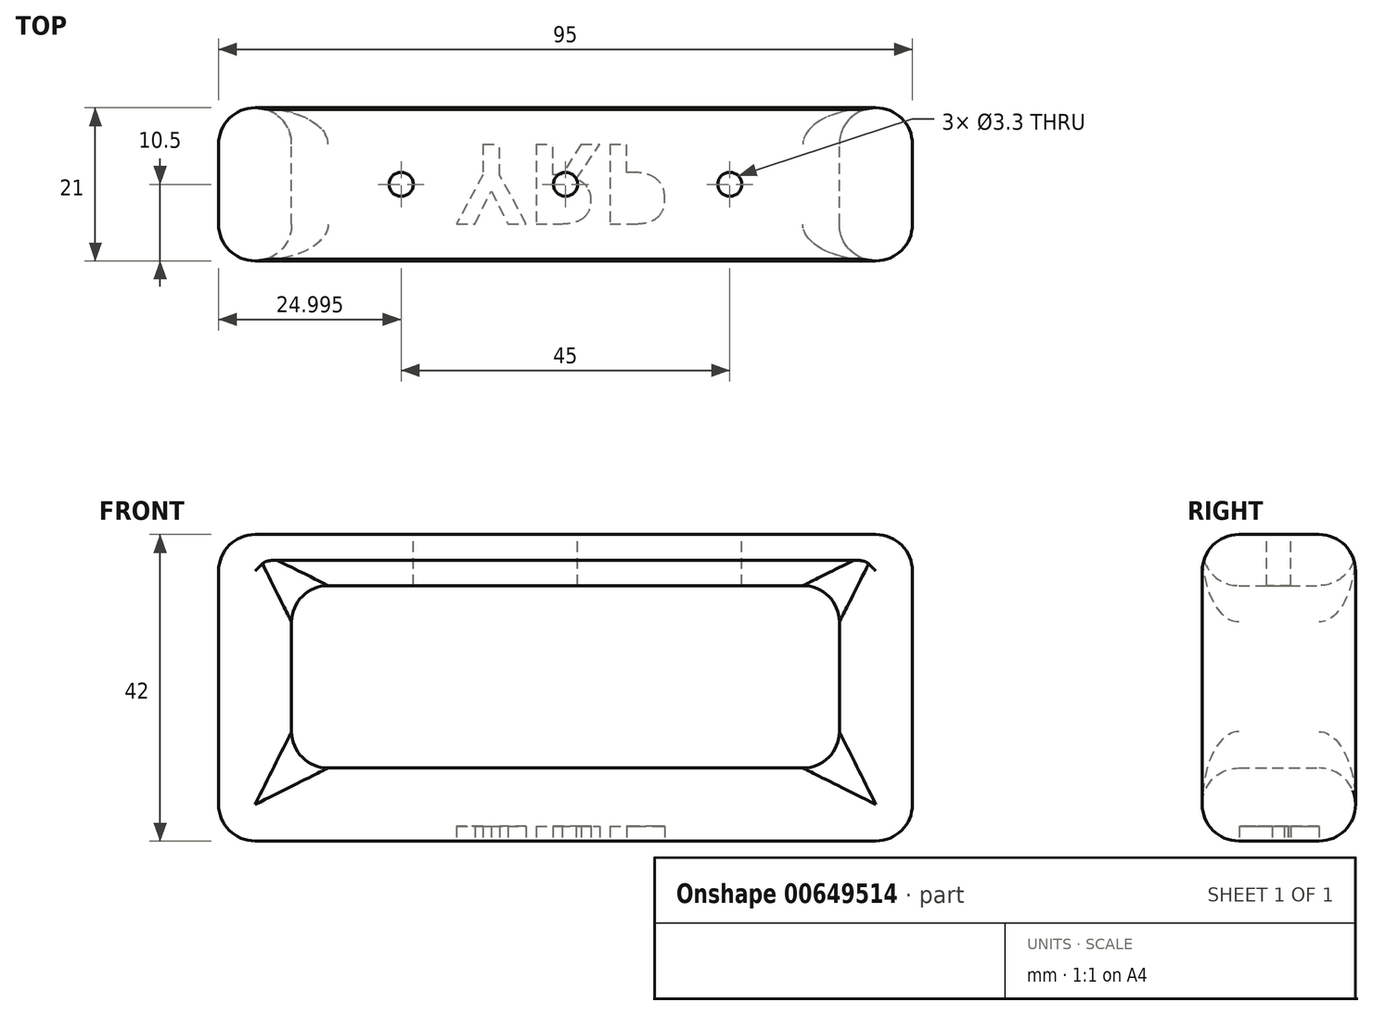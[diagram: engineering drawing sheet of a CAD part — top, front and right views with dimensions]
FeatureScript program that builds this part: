
annotation { "Feature Type Name" : "Feature", "Feature Type Description" : "" }
export const myFeature = defineFeature(function(context is Context, id is Id, definition is map)
    precondition{}
    {
        {
            var Q0;
            Q0=qCreatedBy(makeId("Front.planeOp"),FACE);
            var sketch = newSketch(context, id + "F0", { "sketchPlane" : qUnion([Q0])});
            skLineSegment(sketch, "E0.bottom", {"start": v(-28.82, 7) * mm, "end": v(66.18, 7) * mm});
            skLineSegment(sketch, "E0.top", {"start": v(-28.82, -35) * mm, "end": v(66.18, -35) * mm});
            skLineSegment(sketch, "E0.left", {"start": v(-28.82, 7) * mm, "end": v(-28.82, -35) * mm});
            skLineSegment(sketch, "E0.right", {"start": v(66.18, 7) * mm, "end": v(66.18, -35) * mm});
            skLineSegment(sketch, "E1.bottom", {"start": v(-18.82, 0) * mm, "end": v(56.18, 0) * mm});
            skLineSegment(sketch, "E1.top", {"start": v(-18.82, -25) * mm, "end": v(56.18, -25) * mm});
            skLineSegment(sketch, "E1.left", {"start": v(-18.82, 0) * mm, "end": v(-18.82, -25) * mm});
            skLineSegment(sketch, "E1.right", {"start": v(56.18, 0) * mm, "end": v(56.18, -25) * mm});
            skSolve(sketch);
        }
        {
            var Q0;
            Q0=makeQuery(id+"F0.imprint","IMPRINT",FACE,{"disambiguationData":[TD([[makeQuery(id+"F0.imprint","IMPRINT",EDGE,{"derivedFrom":sQuery(id+"F0.wireOp",EDGE,"E0.bottom")}),-1.0]])]});
            extrude(context, id + "F1", {"entities" : qUnion([Q0]), "depth" : 21 * mm, "offsetDistance" : 25 * mm});
        }
        {
            var Q0;
            Q0=makeQuery(id+"F1.opExtrude","CAP_FACE",FACE,{"disambiguationData":[OSD([sQuery(id+"F0.wireOp",EDGE,"E0.bottom"),sQuery(id+"F0.wireOp",EDGE,"E0.top"),sQuery(id+"F0.wireOp",EDGE,"E0.left"),sQuery(id+"F0.wireOp",EDGE,"E0.right"),sQuery(id+"F0.wireOp",EDGE,"E1.bottom"),sQuery(id+"F0.wireOp",EDGE,"E1.top"),sQuery(id+"F0.wireOp",EDGE,"E1.left"),sQuery(id+"F0.wireOp",EDGE,"E1.right")])],"isStart":false});
            var Q1;
            Q1=makeQuery(id+"F1.opExtrude","CAP_FACE",FACE,{"disambiguationData":[OSD([sQuery(id+"F0.wireOp",EDGE,"E0.bottom"),sQuery(id+"F0.wireOp",EDGE,"E0.top"),sQuery(id+"F0.wireOp",EDGE,"E0.left"),sQuery(id+"F0.wireOp",EDGE,"E0.right"),sQuery(id+"F0.wireOp",EDGE,"E1.bottom"),sQuery(id+"F0.wireOp",EDGE,"E1.top"),sQuery(id+"F0.wireOp",EDGE,"E1.left"),sQuery(id+"F0.wireOp",EDGE,"E1.right")])],"isStart":true});
            var Q2;
            Q2=makeQuery(id+"F1.opExtrude","SWEPT_FACE",FACE,{"disambiguationData":[OSD([sQuery(id+"F0.wireOp",EDGE,"E0.left")])]});
            var Q3;
            Q3=makeQuery(id+"F1.opExtrude","SWEPT_FACE",FACE,{"disambiguationData":[OSD([sQuery(id+"F0.wireOp",EDGE,"E0.top")])]});
            var Q4;
            Q4=makeQuery(id+"F1.opExtrude","SWEPT_FACE",FACE,{"disambiguationData":[OSD([sQuery(id+"F0.wireOp",EDGE,"E0.right")])]});
            var Q5;
            Q5=makeQuery(id+"F1.opExtrude","SWEPT_FACE",FACE,{"disambiguationData":[OSD([sQuery(id+"F0.wireOp",EDGE,"E0.bottom")])]});
            fillet(context, id + "F2", {"entities" : qUnion([Q0, Q1, Q2, Q3, Q4, Q5]), "radius" : 5 * mm, "tangentPropagation" : true, "allowEdgeOverflow" : false});
        }
        {
            var Q0;
            Q0=makeQuery(id+"F1.opExtrude","SWEPT_FACE",FACE,{"disambiguationData":[OSD([sQuery(id+"F0.wireOp",EDGE,"E1.top")])]});
            var Q1;
            {var subQ0=sQuery(id+"F0.wireOp",EDGE,"E1.bottom");Q1=makeQuery(id+"F2.opFillet","BLEND_EDGE",EDGE,{"blendedFrom":[makeQuery(id+"F1.opExtrude","CAP_EDGE",EDGE,{"disambiguationData":[OSD([subQ0])],"isStart":false}),makeQuery(id+"F1.opExtrude","SWEPT_FACE",FACE,{"disambiguationData":[OSD([subQ0])]})],"blendedInto":[makeQuery(id+"F1.opExtrude","SWEPT_FACE",FACE,{"disambiguationData":[OSD([subQ0])]})]});}
            var Q2;
            Q2=makeQuery(id+"F1.opExtrude","SWEPT_FACE",FACE,{"disambiguationData":[OSD([sQuery(id+"F0.wireOp",EDGE,"E1.left")])]});
            var Q3;
            Q3=makeQuery(id+"F1.opExtrude","SWEPT_EDGE",EDGE,{"disambiguationData":[OSD([sQuery(id+"F0.wireOp",EDGE,"E1.bottom"),sQuery(id+"F0.wireOp",EDGE,"E1.right")])]});
            fillet(context, id + "F3", {"entities" : qUnion([Q0, Q1, Q2, Q3]), "radius" : 5 * mm, "tangentPropagation" : true, "allowEdgeOverflow" : false});
        }
        {
            var Q0;
            Q0=makeQuery(id+"F1.opExtrude","SWEPT_FACE",FACE,{"disambiguationData":[OSD([sQuery(id+"F0.wireOp",EDGE,"E0.bottom")])]});
            var sketch = newSketch(context, id + "F4", { "sketchPlane" : qUnion([Q0])});
            skCircle(sketch, "E2", {"center": v(-3.82, -10.5) * mm, "radius": 1.65 * mm});
            skPoint(sketch, "E2.centerSnap0", {"position": v(-23.82, -10.5) * mm});
            skCircle(sketch, "E3", {"center": v(41.18, -10.5) * mm, "radius": 1.65 * mm});
            skCircle(sketch, "E4", {"center": v(18.68, -10.5) * mm, "radius": 1.65 * mm});
            skSolve(sketch);
        }
        {
            var Q0;
            Q0=makeQuery(id+"F4.imprint","IMPRINT",FACE,{"disambiguationData":[TD([[makeQuery(id+"F4.imprint","IMPRINT",EDGE,{"derivedFrom":sQuery(id+"F4.wireOp",EDGE,"E2")}),1.0]])]});
            var Q1;
            Q1=makeQuery(id+"F4.imprint","IMPRINT",FACE,{"disambiguationData":[TD([[makeQuery(id+"F4.imprint","IMPRINT",EDGE,{"derivedFrom":sQuery(id+"F4.wireOp",EDGE,"E3")}),1.0]])]});
            var Q2;
            Q2=makeQuery(id+"F4.imprint","IMPRINT",FACE,{"disambiguationData":[TD([[makeQuery(id+"F4.imprint","IMPRINT",EDGE,{"derivedFrom":sQuery(id+"F4.wireOp",EDGE,"E4")}),1.0]])]});
            extrude(context, id + "F5", {"entities" : qUnion([Q0, Q1, Q2]), "operationType" : NewBodyOperationType.REMOVE, "oppositeDirection" : true, "depth" : 25 * mm, "offsetDistance" : 25 * mm});
        }
        {
            var Q0;
            Q0=makeQuery(id+"F1.opExtrude","SWEPT_FACE",FACE,{"disambiguationData":[OSD([sQuery(id+"F0.wireOp",EDGE,"E0.top")])]});
            var sketch = newSketch(context, id + "F6", { "sketchPlane" : qUnion([Q0])});
            skText(sketch, "E5", { "text": "YRP", "fontName": "NotoSans-Bold.ttf"});
            const initialGuessF6  = {"E5": [0.00375, 0.005, 1, 0, 0.011]};
            skSetInitialGuess(sketch, initialGuessF6);
            skSolve(sketch);
        }
        {
            var Q0;
            Q0 = qSketchRegion(id + "F6", true);
            extrude(context, id + "F7", {"entities" : qUnion([Q0]), "operationType" : NewBodyOperationType.REMOVE, "oppositeDirection" : true, "depth" : 2 * mm, "offsetDistance" : 25 * mm});
        }
        {
            var Q0;
            Q0=makeQuery(id+"F7.boolean.opBoolean","SPLIT",FACE,{"disambiguationData":[TD([makeQuery(id+"F7.opExtrude","SWEPT_FACE",FACE,{"disambiguationData":[OSD([sQuery(id+"F6.wireOp",EDGE,"E5.sketch_text.stroke-9")])]})])],"derivedFrom":makeQuery(id+"F1.opExtrude","SWEPT_FACE",FACE,{"disambiguationData":[OSD([sQuery(id+"F0.wireOp",EDGE,"E0.top")])]})});
            var Q1;
            Q1=makeQuery(id+"F7.boolean.opBoolean","SPLIT",FACE,{"disambiguationData":[TD([makeQuery(id+"F7.opExtrude","SWEPT_FACE",FACE,{"disambiguationData":[OSD([sQuery(id+"F6.wireOp",EDGE,"E5.sketch_text.stroke-28")])]})])],"derivedFrom":makeQuery(id+"F1.opExtrude","SWEPT_FACE",FACE,{"disambiguationData":[OSD([sQuery(id+"F0.wireOp",EDGE,"E0.top")])]})});
            var Q2;
            Q2=makeQuery(id+"F7.boolean.opBoolean","COPY",FACE,{"derivedFrom":makeQuery(id+"F7.opExtrude","CAP_FACE",FACE,{"disambiguationData":[OSD([sQuery(id+"F6.wireOp",EDGE,"E5.sketch_text.stroke-9"),sQuery(id+"F6.wireOp",EDGE,"E5.sketch_text.stroke-10"),sQuery(id+"F6.wireOp",EDGE,"E5.sketch_text.stroke-11"),sQuery(id+"F6.wireOp",EDGE,"E5.sketch_text.stroke-12"),sQuery(id+"F6.wireOp",EDGE,"E5.sketch_text.stroke-13"),sQuery(id+"F6.wireOp",EDGE,"E5.sketch_text.stroke-14"),sQuery(id+"F6.wireOp",EDGE,"E5.sketch_text.stroke-15"),sQuery(id+"F6.wireOp",EDGE,"E5.sketch_text.stroke-16"),sQuery(id+"F6.wireOp",EDGE,"E5.sketch_text.stroke-17"),sQuery(id+"F6.wireOp",EDGE,"E5.sketch_text.stroke-18"),sQuery(id+"F6.wireOp",EDGE,"E5.sketch_text.stroke-19"),sQuery(id+"F6.wireOp",EDGE,"E5.sketch_text.stroke-20"),sQuery(id+"F6.wireOp",EDGE,"E5.sketch_text.stroke-21"),sQuery(id+"F6.wireOp",EDGE,"E5.sketch_text.stroke-22"),sQuery(id+"F6.wireOp",EDGE,"E5.sketch_text.stroke-23"),sQuery(id+"F6.wireOp",EDGE,"E5.sketch_text.stroke-24"),sQuery(id+"F6.wireOp",EDGE,"E5.sketch_text.stroke-25"),sQuery(id+"F6.wireOp",EDGE,"E5.sketch_text.stroke-26"),sQuery(id+"F6.wireOp",EDGE,"E5.sketch_text.stroke-27")])],"isStart":false})});
            extrude(context, id + "F8", {"entities" : qUnion([Q0, Q1]), "operationType" : NewBodyOperationType.REMOVE, "endBound" : BoundingType.UP_TO_SURFACE, "oppositeDirection" : true, "depth" : 25 * mm, "endBoundEntityFace" : qUnion([Q2]), "offsetDistance" : 25 * mm});
        }
    });
